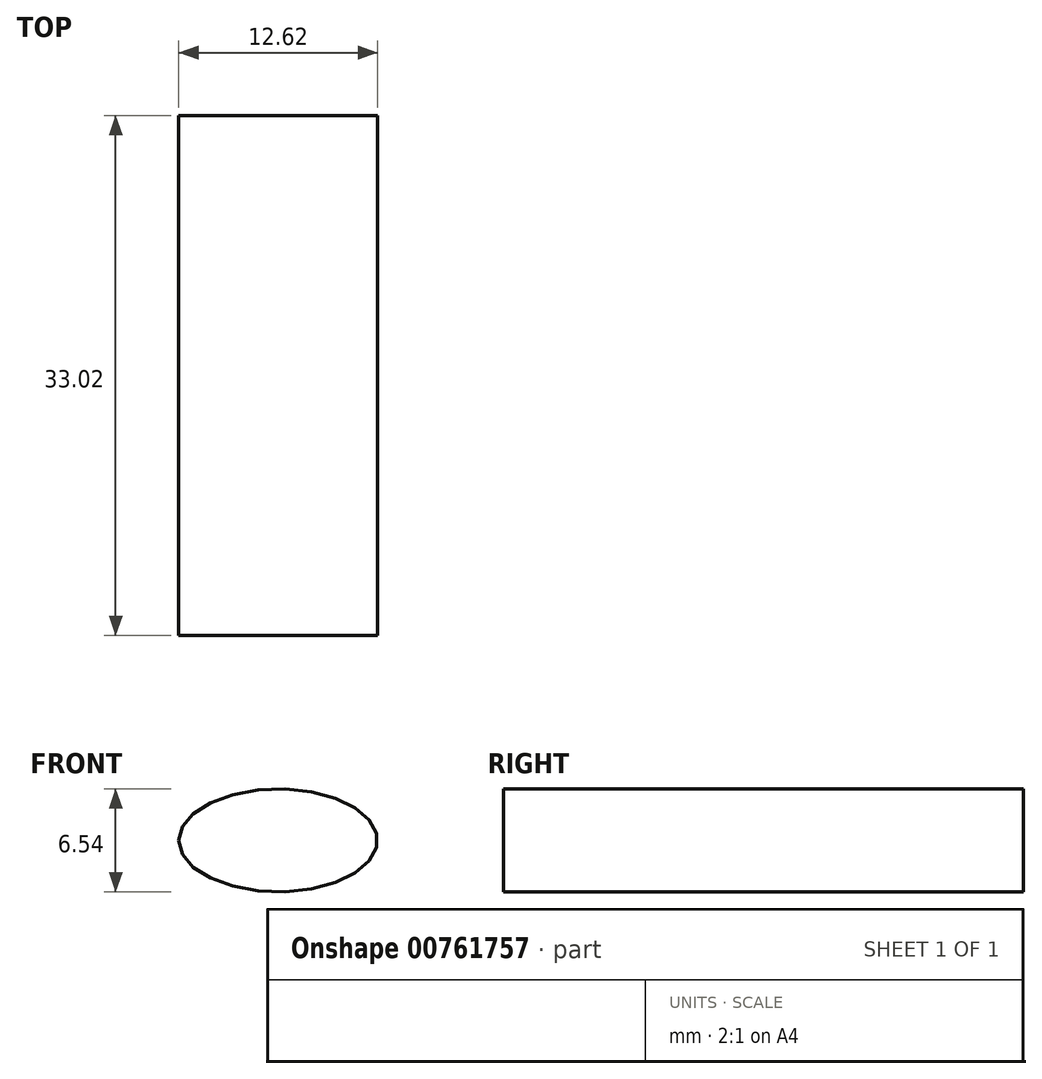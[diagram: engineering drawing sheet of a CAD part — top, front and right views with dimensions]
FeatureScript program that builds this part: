
annotation { "Feature Type Name" : "Feature", "Feature Type Description" : "" }
export const myFeature = defineFeature(function(context is Context, id is Id, definition is map)
    precondition{}
    {
        {
            var Q0;
            Q0=qCreatedBy(makeId("Front.planeOp"),FACE);
            var sketch = newSketch(context, id + "F0", { "sketchPlane" : qUnion([Q0])});
            skEllipse(sketch, "E0", {"center": v(0, 0) * mm, "majorRadius": 6.3 * mm, "minorRadius": 3.27 * mm, "majorAxis": v(-1, 0)});
            skSolve(sketch);
        }
        {
            var Q0;
            Q0=makeQuery(id+"F0.imprint","IMPRINT",FACE,{"disambiguationData":[TD([[makeQuery(id+"F0.imprint","IMPRINT",EDGE,{"derivedFrom":sQuery(id+"F0.wireOp",EDGE,"E0")}),1.0]])]});
            extrude(context, id + "F1", {"entities" : qUnion([Q0]), "depth" : 33.02 * mm, "offsetDistance" : 25.4 * mm});
        }
    });
